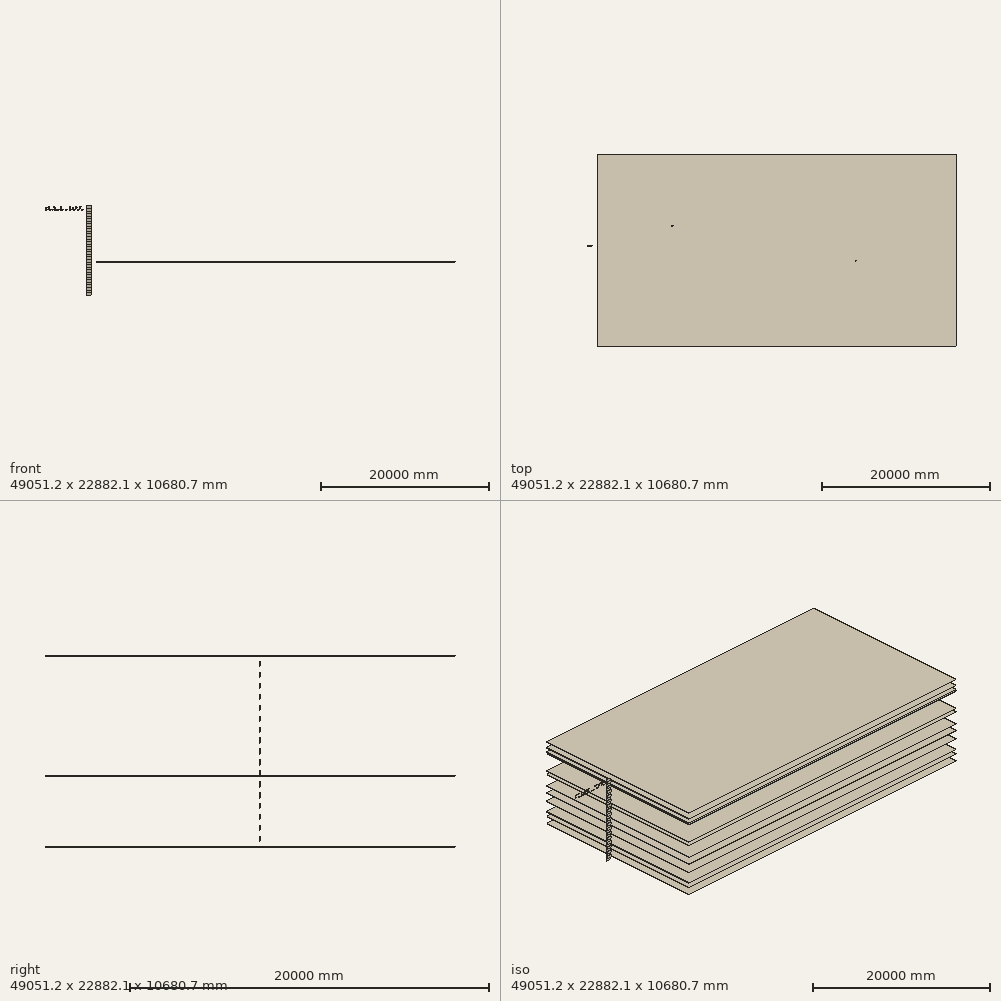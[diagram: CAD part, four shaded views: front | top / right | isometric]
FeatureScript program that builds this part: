
annotation { "Feature Type Name" : "Feature", "Feature Type Description" : "" }
export const myFeature = defineFeature(function(context is Context, id is Id, definition is map)
    precondition{}
    {
        {
            var Q0;
            Q0=qCreatedBy(makeId("Top.planeOp"),FACE);
            var sketch = newSketch(context, id + "F0", { "sketchPlane" : qUnion([Q0])});
            skLineSegment(sketch, "E0.bottom", {"start": v(-13590.57, 10870.04) * mm, "end": v(29302.01, 10870.04) * mm});
            skLineSegment(sketch, "E0.top", {"start": v(-13590.57, -12012.05) * mm, "end": v(29302.01, -12012.05) * mm});
            skLineSegment(sketch, "E0.left", {"start": v(-13590.57, 10870.04) * mm, "end": v(-13590.57, -12012.05) * mm});
            skLineSegment(sketch, "E0.right", {"start": v(29302.01, 10870.04) * mm, "end": v(29302.01, -12012.05) * mm});
            skSolve(sketch);
        }
        {
            var Q0;
            Q0=qSketchRegion(id+"F0",true);
            extrude(context, id + "F1", {"entities" : qUnion([Q0]), "depth" : 12.7 * mm});
        }
        {
            var Q0;
            Q0=makeQuery(id+"F1.opExtrude","SWEPT_BODY",BODY,{"disambiguationData":[OSD([sQuery(id+"F0.wireOp",EDGE,"E0.bottom"),sQuery(id+"F0.wireOp",EDGE,"E0.top"),sQuery(id+"F0.wireOp",EDGE,"E0.left"),sQuery(id+"F0.wireOp",EDGE,"E0.right")])]});
            transform(context, id + "F2", {"entities" : qUnion([Q0]), "transformType" : TransformType.TRANSLATION_3D, "dx" : 0 * mm, "dy" : 0 * mm, "dz" : -762 * mm, "makeCopy" : true});
        }
        {
            var Q0;
            Q0=makeQuery(id+"F1.opExtrude","SWEPT_BODY",BODY,{"disambiguationData":[OSD([sQuery(id+"F0.wireOp",EDGE,"E0.bottom"),sQuery(id+"F0.wireOp",EDGE,"E0.top"),sQuery(id+"F0.wireOp",EDGE,"E0.left"),sQuery(id+"F0.wireOp",EDGE,"E0.right")])]});
            transform(context, id + "F3", {"entities" : qUnion([Q0]), "transformType" : TransformType.TRANSLATION_3D, "dx" : 0 * mm, "dy" : 0 * mm, "dz" : -1295.4 * mm, "makeCopy" : true});
        }
        {
            var Q0;
            Q0=makeQuery(id+"F1.opExtrude","SWEPT_BODY",BODY,{"disambiguationData":[OSD([sQuery(id+"F0.wireOp",EDGE,"E0.bottom"),sQuery(id+"F0.wireOp",EDGE,"E0.top"),sQuery(id+"F0.wireOp",EDGE,"E0.left"),sQuery(id+"F0.wireOp",EDGE,"E0.right")])]});
            transform(context, id + "F4", {"entities" : qUnion([Q0]), "transformType" : TransformType.TRANSLATION_3D, "dx" : 0 * mm, "dy" : 0 * mm, "dz" : -1524 * mm, "makeCopy" : true});
        }
        {
            var Q0;
            Q0=makeQuery(id+"F1.opExtrude","SWEPT_BODY",BODY,{"disambiguationData":[OSD([sQuery(id+"F0.wireOp",EDGE,"E0.bottom"),sQuery(id+"F0.wireOp",EDGE,"E0.top"),sQuery(id+"F0.wireOp",EDGE,"E0.left"),sQuery(id+"F0.wireOp",EDGE,"E0.right")])]});
            transform(context, id + "F5", {"entities" : qUnion([Q0]), "transformType" : TransformType.TRANSLATION_3D, "dx" : 0 * mm, "dy" : 0 * mm, "dz" : -3810 * mm, "makeCopy" : true});
        }
        {
            var Q0;
            Q0=makeQuery(id+"F1.opExtrude","SWEPT_BODY",BODY,{"disambiguationData":[OSD([sQuery(id+"F0.wireOp",EDGE,"E0.bottom"),sQuery(id+"F0.wireOp",EDGE,"E0.top"),sQuery(id+"F0.wireOp",EDGE,"E0.left"),sQuery(id+"F0.wireOp",EDGE,"E0.right")])]});
            transform(context, id + "F6", {"entities" : qUnion([Q0]), "transformType" : TransformType.TRANSLATION_3D, "dx" : 0 * mm, "dy" : 0 * mm, "dz" : -4267.2 * mm, "makeCopy" : true});
        }
        {
            var Q0;
            Q0=makeQuery(id+"F1.opExtrude","SWEPT_BODY",BODY,{"disambiguationData":[OSD([sQuery(id+"F0.wireOp",EDGE,"E0.bottom"),sQuery(id+"F0.wireOp",EDGE,"E0.top"),sQuery(id+"F0.wireOp",EDGE,"E0.left"),sQuery(id+"F0.wireOp",EDGE,"E0.right")])]});
            transform(context, id + "F7", {"entities" : qUnion([Q0]), "transformType" : TransformType.TRANSLATION_3D, "dx" : 0 * mm, "dy" : 0 * mm, "dz" : -5791.2 * mm, "makeCopy" : true});
        }
        {
            var Q0;
            Q0=makeQuery(id+"F1.opExtrude","SWEPT_BODY",BODY,{"disambiguationData":[OSD([sQuery(id+"F0.wireOp",EDGE,"E0.bottom"),sQuery(id+"F0.wireOp",EDGE,"E0.top"),sQuery(id+"F0.wireOp",EDGE,"E0.left"),sQuery(id+"F0.wireOp",EDGE,"E0.right")])]});
            transform(context, id + "F8", {"entities" : qUnion([Q0]), "transformType" : TransformType.TRANSLATION_3D, "dx" : 0 * mm, "dy" : 0 * mm, "dz" : -6705.6 * mm, "makeCopy" : true});
        }
        {
            var Q0;
            Q0=makeQuery(id+"F1.opExtrude","SWEPT_BODY",BODY,{"disambiguationData":[OSD([sQuery(id+"F0.wireOp",EDGE,"E0.bottom"),sQuery(id+"F0.wireOp",EDGE,"E0.top"),sQuery(id+"F0.wireOp",EDGE,"E0.left"),sQuery(id+"F0.wireOp",EDGE,"E0.right")])]});
            transform(context, id + "F9", {"entities" : qUnion([Q0]), "transformType" : TransformType.TRANSLATION_3D, "dx" : 0 * mm, "dy" : 0 * mm, "dz" : -7772.4 * mm, "makeCopy" : true});
        }
        {
            var Q0;
            Q0=makeQuery(id+"F1.opExtrude","SWEPT_BODY",BODY,{"disambiguationData":[OSD([sQuery(id+"F0.wireOp",EDGE,"E0.bottom"),sQuery(id+"F0.wireOp",EDGE,"E0.top"),sQuery(id+"F0.wireOp",EDGE,"E0.left"),sQuery(id+"F0.wireOp",EDGE,"E0.right")])]});
            transform(context, id + "F10", {"entities" : qUnion([Q0]), "transformType" : TransformType.TRANSLATION_3D, "dx" : 0 * mm, "dy" : 0 * mm, "dz" : -9144 * mm, "makeCopy" : true});
        }
        {
            var Q0;
            Q0=makeQuery(id+"F1.opExtrude","SWEPT_BODY",BODY,{"disambiguationData":[OSD([sQuery(id+"F0.wireOp",EDGE,"E0.bottom"),sQuery(id+"F0.wireOp",EDGE,"E0.top"),sQuery(id+"F0.wireOp",EDGE,"E0.left"),sQuery(id+"F0.wireOp",EDGE,"E0.right")])]});
            transform(context, id + "F11", {"entities" : qUnion([Q0]), "transformType" : TransformType.TRANSLATION_3D, "dx" : 0 * mm, "dy" : 0 * mm, "dz" : -9753.6 * mm, "makeCopy" : true});
        }
        {
            var Q0;
            Q0=makeQuery(id+"F1.opExtrude","SWEPT_BODY",BODY,{"disambiguationData":[OSD([sQuery(id+"F0.wireOp",EDGE,"E0.bottom"),sQuery(id+"F0.wireOp",EDGE,"E0.top"),sQuery(id+"F0.wireOp",EDGE,"E0.left"),sQuery(id+"F0.wireOp",EDGE,"E0.right")])]});
            transform(context, id + "F12", {"entities" : qUnion([Q0]), "transformType" : TransformType.TRANSLATION_3D, "dx" : 0 * mm, "dy" : 0 * mm, "dz" : -10668 * mm, "makeCopy" : true});
        }
        {
            var Q0;
            Q0=makeQuery(id+"F1.opExtrude","CAP_FACE",FACE,{"disambiguationData":[OSD([sQuery(id+"F0.wireOp",EDGE,"E0.bottom"),sQuery(id+"F0.wireOp",EDGE,"E0.top"),sQuery(id+"F0.wireOp",EDGE,"E0.left"),sQuery(id+"F0.wireOp",EDGE,"E0.right")])],"isStart":false});
            var sketch = newSketch(context, id + "F13", { "sketchPlane" : qUnion([Q0])});
            skCircle(sketch, "E1", {"center": v(-4667.52, 2370.02) * mm, "radius": 76.2 * mm});
            skCircle(sketch, "E2", {"center": v(17228.5, -1797.32) * mm, "radius": 76.2 * mm});
            skSolve(sketch);
        }
        {
            var Q0;
            Q0=qSketchRegion(id+"F13",true);
            extrude(context, id + "F14", {"entities" : qUnion([Q0]), "operationType" : NewBodyOperationType.REMOVE, "endBound" : BoundingType.THROUGH_ALL, "oppositeDirection" : true, "depth" : 30.48 * mm});
        }
        {
            var Q0;
            Q0=qCreatedBy(makeId("Front.planeOp"),FACE);
            var sketch = newSketch(context, id + "F15", { "sketchPlane" : qUnion([Q0])});
            skLineSegment(sketch, "E3.bottom", {"start": v(-14200.17, 0) * mm, "end": v(-14809.77, 0) * mm});
            skLineSegment(sketch, "E3.top", {"start": v(-14200.17, -304.8) * mm, "end": v(-14809.77, -304.8) * mm});
            skLineSegment(sketch, "E3.left", {"start": v(-14200.17, 0) * mm, "end": v(-14200.17, -304.8) * mm});
            skLineSegment(sketch, "E3.right", {"start": v(-14809.77, 0) * mm, "end": v(-14809.77, -304.8) * mm});
            skLineSegment(sketch, "E4.0.1.0", {"start": v(-14200.17, -609.6) * mm, "end": v(-14809.77, -609.6) * mm});
            skLineSegment(sketch, "E4.0.1.1", {"start": v(-14200.17, -304.8) * mm, "end": v(-14200.17, -609.6) * mm});
            skLineSegment(sketch, "E4.0.1.2", {"start": v(-14809.77, -304.8) * mm, "end": v(-14809.77, -609.6) * mm});
            skLineSegment(sketch, "E4.direction1", {"start": v(-14809.77, -304.8) * mm, "end": v(-14600.97, -304.8) * mm, "construction": true});
            skLineSegment(sketch, "E4.direction2", {"start": v(-14809.77, -304.8) * mm, "end": v(-14809.77, -609.6) * mm, "construction": true});
            skLineSegment(sketch, "E5.0.0.2", {"start": v(-14200.17, -914.4) * mm, "end": v(-14809.77, -914.4) * mm});
            skLineSegment(sketch, "E5.3.0.2", {"start": v(-14200.17, -609.6) * mm, "end": v(-14200.17, -914.4) * mm});
            skLineSegment(sketch, "E5.6.0.2", {"start": v(-14809.77, -609.6) * mm, "end": v(-14809.77, -914.4) * mm});
            skLineSegment(sketch, "E5.0.0.3", {"start": v(-14200.17, -1219.2) * mm, "end": v(-14809.77, -1219.2) * mm});
            skLineSegment(sketch, "E5.3.0.3", {"start": v(-14200.17, -914.4) * mm, "end": v(-14200.17, -1219.2) * mm});
            skLineSegment(sketch, "E5.6.0.3", {"start": v(-14809.77, -914.4) * mm, "end": v(-14809.77, -1219.2) * mm});
            skLineSegment(sketch, "E5.0.0.4", {"start": v(-14200.17, -1524) * mm, "end": v(-14809.77, -1524) * mm});
            skLineSegment(sketch, "E5.3.0.4", {"start": v(-14200.17, -1219.2) * mm, "end": v(-14200.17, -1524) * mm});
            skLineSegment(sketch, "E5.6.0.4", {"start": v(-14809.77, -1219.2) * mm, "end": v(-14809.77, -1524) * mm});
            skLineSegment(sketch, "E5.0.0.5", {"start": v(-14200.17, -1828.8) * mm, "end": v(-14809.77, -1828.8) * mm});
            skLineSegment(sketch, "E5.3.0.5", {"start": v(-14200.17, -1524) * mm, "end": v(-14200.17, -1828.8) * mm});
            skLineSegment(sketch, "E5.6.0.5", {"start": v(-14809.77, -1524) * mm, "end": v(-14809.77, -1828.8) * mm});
            skLineSegment(sketch, "E5.0.0.6", {"start": v(-14200.17, -2133.6) * mm, "end": v(-14809.77, -2133.6) * mm});
            skLineSegment(sketch, "E5.3.0.6", {"start": v(-14200.17, -1828.8) * mm, "end": v(-14200.17, -2133.6) * mm});
            skLineSegment(sketch, "E5.6.0.6", {"start": v(-14809.77, -1828.8) * mm, "end": v(-14809.77, -2133.6) * mm});
            skLineSegment(sketch, "E5.0.0.7", {"start": v(-14200.17, -2438.4) * mm, "end": v(-14809.77, -2438.4) * mm});
            skLineSegment(sketch, "E5.3.0.7", {"start": v(-14200.17, -2133.6) * mm, "end": v(-14200.17, -2438.4) * mm});
            skLineSegment(sketch, "E5.6.0.7", {"start": v(-14809.77, -2133.6) * mm, "end": v(-14809.77, -2438.4) * mm});
            skLineSegment(sketch, "E5.0.0.8", {"start": v(-14200.17, -2743.2) * mm, "end": v(-14809.77, -2743.2) * mm});
            skLineSegment(sketch, "E5.3.0.8", {"start": v(-14200.17, -2438.4) * mm, "end": v(-14200.17, -2743.2) * mm});
            skLineSegment(sketch, "E5.6.0.8", {"start": v(-14809.77, -2438.4) * mm, "end": v(-14809.77, -2743.2) * mm});
            skLineSegment(sketch, "E5.0.0.9", {"start": v(-14200.17, -3048) * mm, "end": v(-14809.77, -3048) * mm});
            skLineSegment(sketch, "E5.3.0.9", {"start": v(-14200.17, -2743.2) * mm, "end": v(-14200.17, -3048) * mm});
            skLineSegment(sketch, "E5.6.0.9", {"start": v(-14809.77, -2743.2) * mm, "end": v(-14809.77, -3048) * mm});
            skLineSegment(sketch, "E5.0.0.10", {"start": v(-14200.17, -3352.8) * mm, "end": v(-14809.77, -3352.8) * mm});
            skLineSegment(sketch, "E5.3.0.10", {"start": v(-14200.17, -3048) * mm, "end": v(-14200.17, -3352.8) * mm});
            skLineSegment(sketch, "E5.6.0.10", {"start": v(-14809.77, -3048) * mm, "end": v(-14809.77, -3352.8) * mm});
            skLineSegment(sketch, "E5.0.0.11", {"start": v(-14200.17, -3657.6) * mm, "end": v(-14809.77, -3657.6) * mm});
            skLineSegment(sketch, "E5.3.0.11", {"start": v(-14200.17, -3352.8) * mm, "end": v(-14200.17, -3657.6) * mm});
            skLineSegment(sketch, "E5.6.0.11", {"start": v(-14809.77, -3352.8) * mm, "end": v(-14809.77, -3657.6) * mm});
            skLineSegment(sketch, "E5.0.0.12", {"start": v(-14200.17, -3962.4) * mm, "end": v(-14809.77, -3962.4) * mm});
            skLineSegment(sketch, "E5.3.0.12", {"start": v(-14200.17, -3657.6) * mm, "end": v(-14200.17, -3962.4) * mm});
            skLineSegment(sketch, "E5.6.0.12", {"start": v(-14809.77, -3657.6) * mm, "end": v(-14809.77, -3962.4) * mm});
            skLineSegment(sketch, "E5.0.0.13", {"start": v(-14200.17, -4267.2) * mm, "end": v(-14809.77, -4267.2) * mm});
            skLineSegment(sketch, "E5.3.0.13", {"start": v(-14200.17, -3962.4) * mm, "end": v(-14200.17, -4267.2) * mm});
            skLineSegment(sketch, "E5.6.0.13", {"start": v(-14809.77, -3962.4) * mm, "end": v(-14809.77, -4267.2) * mm});
            skLineSegment(sketch, "E5.0.0.14", {"start": v(-14200.17, -4572) * mm, "end": v(-14809.77, -4572) * mm});
            skLineSegment(sketch, "E5.3.0.14", {"start": v(-14200.17, -4267.2) * mm, "end": v(-14200.17, -4572) * mm});
            skLineSegment(sketch, "E5.6.0.14", {"start": v(-14809.77, -4267.2) * mm, "end": v(-14809.77, -4572) * mm});
            skLineSegment(sketch, "E5.0.0.15", {"start": v(-14200.17, -4876.8) * mm, "end": v(-14809.77, -4876.8) * mm});
            skLineSegment(sketch, "E5.3.0.15", {"start": v(-14200.17, -4572) * mm, "end": v(-14200.17, -4876.8) * mm});
            skLineSegment(sketch, "E5.6.0.15", {"start": v(-14809.77, -4572) * mm, "end": v(-14809.77, -4876.8) * mm});
            skLineSegment(sketch, "E5.0.0.16", {"start": v(-14200.17, -5181.6) * mm, "end": v(-14809.77, -5181.6) * mm});
            skLineSegment(sketch, "E5.3.0.16", {"start": v(-14200.17, -4876.8) * mm, "end": v(-14200.17, -5181.6) * mm});
            skLineSegment(sketch, "E5.6.0.16", {"start": v(-14809.77, -4876.8) * mm, "end": v(-14809.77, -5181.6) * mm});
            skLineSegment(sketch, "E5.0.0.17", {"start": v(-14200.17, -5486.4) * mm, "end": v(-14809.77, -5486.4) * mm});
            skLineSegment(sketch, "E5.3.0.17", {"start": v(-14200.17, -5181.6) * mm, "end": v(-14200.17, -5486.4) * mm});
            skLineSegment(sketch, "E5.6.0.17", {"start": v(-14809.77, -5181.6) * mm, "end": v(-14809.77, -5486.4) * mm});
            skLineSegment(sketch, "E5.0.0.18", {"start": v(-14200.17, -5791.2) * mm, "end": v(-14809.77, -5791.2) * mm});
            skLineSegment(sketch, "E5.3.0.18", {"start": v(-14200.17, -5486.4) * mm, "end": v(-14200.17, -5791.2) * mm});
            skLineSegment(sketch, "E5.6.0.18", {"start": v(-14809.77, -5486.4) * mm, "end": v(-14809.77, -5791.2) * mm});
            skLineSegment(sketch, "E5.0.0.19", {"start": v(-14200.17, -6096) * mm, "end": v(-14809.77, -6096) * mm});
            skLineSegment(sketch, "E5.3.0.19", {"start": v(-14200.17, -5791.2) * mm, "end": v(-14200.17, -6096) * mm});
            skLineSegment(sketch, "E5.6.0.19", {"start": v(-14809.77, -5791.2) * mm, "end": v(-14809.77, -6096) * mm});
            skLineSegment(sketch, "E6.0.0.20", {"start": v(-14200.17, -6400.8) * mm, "end": v(-14809.77, -6400.8) * mm});
            skLineSegment(sketch, "E6.3.0.20", {"start": v(-14200.17, -6096) * mm, "end": v(-14200.17, -6400.8) * mm});
            skLineSegment(sketch, "E6.6.0.20", {"start": v(-14809.77, -6096) * mm, "end": v(-14809.77, -6400.8) * mm});
            skLineSegment(sketch, "E6.0.0.21", {"start": v(-14200.17, -6705.6) * mm, "end": v(-14809.77, -6705.6) * mm});
            skLineSegment(sketch, "E6.3.0.21", {"start": v(-14200.17, -6400.8) * mm, "end": v(-14200.17, -6705.6) * mm});
            skLineSegment(sketch, "E6.6.0.21", {"start": v(-14809.77, -6400.8) * mm, "end": v(-14809.77, -6705.6) * mm});
            skLineSegment(sketch, "E6.0.0.22", {"start": v(-14200.17, -7010.4) * mm, "end": v(-14809.77, -7010.4) * mm});
            skLineSegment(sketch, "E6.3.0.22", {"start": v(-14200.17, -6705.6) * mm, "end": v(-14200.17, -7010.4) * mm});
            skLineSegment(sketch, "E6.6.0.22", {"start": v(-14809.77, -6705.6) * mm, "end": v(-14809.77, -7010.4) * mm});
            skLineSegment(sketch, "E6.0.0.23", {"start": v(-14200.17, -7315.2) * mm, "end": v(-14809.77, -7315.2) * mm});
            skLineSegment(sketch, "E6.3.0.23", {"start": v(-14200.17, -7010.4) * mm, "end": v(-14200.17, -7315.2) * mm});
            skLineSegment(sketch, "E6.6.0.23", {"start": v(-14809.77, -7010.4) * mm, "end": v(-14809.77, -7315.2) * mm});
            skLineSegment(sketch, "E6.0.0.24", {"start": v(-14200.17, -7620) * mm, "end": v(-14809.77, -7620) * mm});
            skLineSegment(sketch, "E6.3.0.24", {"start": v(-14200.17, -7315.2) * mm, "end": v(-14200.17, -7620) * mm});
            skLineSegment(sketch, "E6.6.0.24", {"start": v(-14809.77, -7315.2) * mm, "end": v(-14809.77, -7620) * mm});
            skLineSegment(sketch, "E6.0.0.25", {"start": v(-14200.17, -7924.8) * mm, "end": v(-14809.77, -7924.8) * mm});
            skLineSegment(sketch, "E6.3.0.25", {"start": v(-14200.17, -7620) * mm, "end": v(-14200.17, -7924.8) * mm});
            skLineSegment(sketch, "E6.6.0.25", {"start": v(-14809.77, -7620) * mm, "end": v(-14809.77, -7924.8) * mm});
            skLineSegment(sketch, "E6.0.0.26", {"start": v(-14200.17, -8229.6) * mm, "end": v(-14809.77, -8229.6) * mm});
            skLineSegment(sketch, "E6.3.0.26", {"start": v(-14200.17, -7924.8) * mm, "end": v(-14200.17, -8229.6) * mm});
            skLineSegment(sketch, "E6.6.0.26", {"start": v(-14809.77, -7924.8) * mm, "end": v(-14809.77, -8229.6) * mm});
            skLineSegment(sketch, "E6.0.0.27", {"start": v(-14200.17, -8534.4) * mm, "end": v(-14809.77, -8534.4) * mm});
            skLineSegment(sketch, "E6.3.0.27", {"start": v(-14200.17, -8229.6) * mm, "end": v(-14200.17, -8534.4) * mm});
            skLineSegment(sketch, "E6.6.0.27", {"start": v(-14809.77, -8229.6) * mm, "end": v(-14809.77, -8534.4) * mm});
            skLineSegment(sketch, "E6.0.0.28", {"start": v(-14200.17, -8839.2) * mm, "end": v(-14809.77, -8839.2) * mm});
            skLineSegment(sketch, "E6.3.0.28", {"start": v(-14200.17, -8534.4) * mm, "end": v(-14200.17, -8839.2) * mm});
            skLineSegment(sketch, "E6.6.0.28", {"start": v(-14809.77, -8534.4) * mm, "end": v(-14809.77, -8839.2) * mm});
            skLineSegment(sketch, "E6.0.0.29", {"start": v(-14200.17, -9144) * mm, "end": v(-14809.77, -9144) * mm});
            skLineSegment(sketch, "E6.3.0.29", {"start": v(-14200.17, -8839.2) * mm, "end": v(-14200.17, -9144) * mm});
            skLineSegment(sketch, "E6.6.0.29", {"start": v(-14809.77, -8839.2) * mm, "end": v(-14809.77, -9144) * mm});
            skLineSegment(sketch, "E6.0.0.30", {"start": v(-14200.17, -9448.8) * mm, "end": v(-14809.77, -9448.8) * mm});
            skLineSegment(sketch, "E6.3.0.30", {"start": v(-14200.17, -9144) * mm, "end": v(-14200.17, -9448.8) * mm});
            skLineSegment(sketch, "E6.6.0.30", {"start": v(-14809.77, -9144) * mm, "end": v(-14809.77, -9448.8) * mm});
            skLineSegment(sketch, "E6.0.0.31", {"start": v(-14200.17, -9753.6) * mm, "end": v(-14809.77, -9753.6) * mm});
            skLineSegment(sketch, "E6.3.0.31", {"start": v(-14200.17, -9448.8) * mm, "end": v(-14200.17, -9753.6) * mm});
            skLineSegment(sketch, "E6.6.0.31", {"start": v(-14809.77, -9448.8) * mm, "end": v(-14809.77, -9753.6) * mm});
            skLineSegment(sketch, "E6.0.0.32", {"start": v(-14200.17, -10058.4) * mm, "end": v(-14809.77, -10058.4) * mm});
            skLineSegment(sketch, "E6.3.0.32", {"start": v(-14200.17, -9753.6) * mm, "end": v(-14200.17, -10058.4) * mm});
            skLineSegment(sketch, "E6.6.0.32", {"start": v(-14809.77, -9753.6) * mm, "end": v(-14809.77, -10058.4) * mm});
            skLineSegment(sketch, "E6.0.0.33", {"start": v(-14200.17, -10363.2) * mm, "end": v(-14809.77, -10363.2) * mm});
            skLineSegment(sketch, "E6.3.0.33", {"start": v(-14200.17, -10058.4) * mm, "end": v(-14200.17, -10363.2) * mm});
            skLineSegment(sketch, "E6.6.0.33", {"start": v(-14809.77, -10058.4) * mm, "end": v(-14809.77, -10363.2) * mm});
            skLineSegment(sketch, "E6.0.0.34", {"start": v(-14200.17, -10668) * mm, "end": v(-14809.77, -10668) * mm});
            skLineSegment(sketch, "E6.3.0.34", {"start": v(-14200.17, -10363.2) * mm, "end": v(-14200.17, -10668) * mm});
            skLineSegment(sketch, "E6.6.0.34", {"start": v(-14809.77, -10363.2) * mm, "end": v(-14809.77, -10668) * mm});
            skSolve(sketch);
        }
        {
            var Q0;
            Q0=qCreatedBy(makeId("Front.planeOp"),FACE);
            var sketch = newSketch(context, id + "F16", { "sketchPlane" : qUnion([Q0])});
            skText(sketch, "E7", { "text": "SCALE 1 FOOT", "fontName": "Tinos-Regular.ttf"});
            const initialGuessF16  = {"E7": [-19.79556, -0.4993, 1, 0, 0.4993]};
            skSetInitialGuess(sketch, initialGuessF16);
            skSolve(sketch);
        }
        {
            var Q0;
            Q0=makeQuery(id+"F16.imprint","IMPRINT",FACE,{"disambiguationData":[TD([[makeQuery(id+"F16.imprint","IMPRINT",EDGE,{"derivedFrom":sQuery(id+"F16.wireOp",EDGE,"E7.sketch_text.stroke-0")}),-1.0]])]});
            var Q1;
            Q1=makeQuery(id+"F16.imprint","IMPRINT",FACE,{"disambiguationData":[TD([[makeQuery(id+"F16.imprint","IMPRINT",EDGE,{"derivedFrom":sQuery(id+"F16.wireOp",EDGE,"E7.sketch_text.stroke-36")}),-1.0]])]});
            var Q2;
            Q2=makeQuery(id+"F16.imprint","IMPRINT",FACE,{"disambiguationData":[TD([[makeQuery(id+"F16.imprint","IMPRINT",EDGE,{"derivedFrom":sQuery(id+"F16.wireOp",EDGE,"E7.sketch_text.stroke-56")}),-1.0]])]});
            var Q3;
            Q3=makeQuery(id+"F16.imprint","IMPRINT",FACE,{"disambiguationData":[TD([[makeQuery(id+"F16.imprint","IMPRINT",EDGE,{"derivedFrom":sQuery(id+"F16.wireOp",EDGE,"E7.sketch_text.stroke-75")}),-1.0]])]});
            var Q4;
            Q4=makeQuery(id+"F16.imprint","IMPRINT",FACE,{"disambiguationData":[TD([[makeQuery(id+"F16.imprint","IMPRINT",EDGE,{"derivedFrom":sQuery(id+"F16.wireOp",EDGE,"E7.sketch_text.stroke-90")}),-1.0]])]});
            var Q5;
            Q5=makeQuery(id+"F16.imprint","IMPRINT",FACE,{"disambiguationData":[TD([[makeQuery(id+"F16.imprint","IMPRINT",EDGE,{"derivedFrom":sQuery(id+"F16.wireOp",EDGE,"E7.sketch_text.stroke-116")}),-1.0]])]});
            var Q6;
            Q6=makeQuery(id+"F16.imprint","IMPRINT",FACE,{"disambiguationData":[TD([[makeQuery(id+"F16.imprint","IMPRINT",EDGE,{"derivedFrom":sQuery(id+"F16.wireOp",EDGE,"E7.sketch_text.stroke-165")}),-1.0]])]});
            var Q7;
            Q7=makeQuery(id+"F16.imprint","IMPRINT",FACE,{"disambiguationData":[TD([[makeQuery(id+"F16.imprint","IMPRINT",EDGE,{"derivedFrom":sQuery(id+"F16.wireOp",EDGE,"E7.sketch_text.stroke-180")}),-1.0]])]});
            var Q8;
            Q8=makeQuery(id+"F16.imprint","IMPRINT",FACE,{"disambiguationData":[TD([[makeQuery(id+"F16.imprint","IMPRINT",EDGE,{"derivedFrom":sQuery(id+"F16.wireOp",EDGE,"E7.sketch_text.stroke-150")}),-1.0]])]});
            var Q9;
            Q9=makeQuery(id+"F16.imprint","IMPRINT",FACE,{"disambiguationData":[TD([[makeQuery(id+"F16.imprint","IMPRINT",EDGE,{"derivedFrom":sQuery(id+"F16.wireOp",EDGE,"E7.sketch_text.stroke-127")}),-1.0]])]});
            extrude(context, id + "F17", {"entities" : qUnion([Q0, Q1, Q2, Q3, Q4, Q5, Q6, Q7, Q8, Q9]), "depth" : 30.48 * mm});
        }
        {
            var Q0;
            Q0=makeQuery(id+"F15.imprint","IMPRINT",FACE,{"disambiguationData":[TD([[makeQuery(id+"F15.imprint","IMPRINT",EDGE,{"derivedFrom":sQuery(id+"F15.wireOp",EDGE,"E3.bottom")}),1.0]])]});
            var Q1;
            Q1=makeQuery(id+"F15.imprint","IMPRINT",FACE,{"disambiguationData":[TD([[makeQuery(id+"F15.imprint","IMPRINT",EDGE,{"derivedFrom":sQuery(id+"F15.wireOp",EDGE,"E4.0.1.0")}),1.0]])]});
            var Q2;
            Q2=makeQuery(id+"F15.imprint","IMPRINT",FACE,{"disambiguationData":[TD([[makeQuery(id+"F15.imprint","IMPRINT",EDGE,{"derivedFrom":sQuery(id+"F15.wireOp",EDGE,"E5.0.0.3")}),1.0]])]});
            var Q3;
            Q3=makeQuery(id+"F15.imprint","IMPRINT",FACE,{"disambiguationData":[TD([[makeQuery(id+"F15.imprint","IMPRINT",EDGE,{"derivedFrom":sQuery(id+"F15.wireOp",EDGE,"E5.0.0.5")}),1.0]])]});
            var Q4;
            Q4=makeQuery(id+"F15.imprint","IMPRINT",FACE,{"disambiguationData":[TD([[makeQuery(id+"F15.imprint","IMPRINT",EDGE,{"derivedFrom":sQuery(id+"F15.wireOp",EDGE,"E5.0.0.7")}),1.0]])]});
            var Q5;
            Q5=makeQuery(id+"F15.imprint","IMPRINT",FACE,{"disambiguationData":[TD([[makeQuery(id+"F15.imprint","IMPRINT",EDGE,{"derivedFrom":sQuery(id+"F15.wireOp",EDGE,"E5.0.0.9")}),1.0]])]});
            var Q6;
            Q6=makeQuery(id+"F15.imprint","IMPRINT",FACE,{"disambiguationData":[TD([[makeQuery(id+"F15.imprint","IMPRINT",EDGE,{"derivedFrom":sQuery(id+"F15.wireOp",EDGE,"E5.0.0.11")}),1.0]])]});
            var Q7;
            Q7=makeQuery(id+"F15.imprint","IMPRINT",FACE,{"disambiguationData":[TD([[makeQuery(id+"F15.imprint","IMPRINT",EDGE,{"derivedFrom":sQuery(id+"F15.wireOp",EDGE,"E5.0.0.13")}),1.0]])]});
            var Q8;
            Q8=makeQuery(id+"F15.imprint","IMPRINT",FACE,{"disambiguationData":[TD([[makeQuery(id+"F15.imprint","IMPRINT",EDGE,{"derivedFrom":sQuery(id+"F15.wireOp",EDGE,"E5.0.0.15")}),1.0]])]});
            var Q9;
            Q9=makeQuery(id+"F15.imprint","IMPRINT",FACE,{"disambiguationData":[TD([[makeQuery(id+"F15.imprint","IMPRINT",EDGE,{"derivedFrom":sQuery(id+"F15.wireOp",EDGE,"E5.0.0.17")}),1.0]])]});
            var Q10;
            Q10=makeQuery(id+"F15.imprint","IMPRINT",FACE,{"disambiguationData":[TD([[makeQuery(id+"F15.imprint","IMPRINT",EDGE,{"derivedFrom":sQuery(id+"F15.wireOp",EDGE,"E5.0.0.19")}),1.0]])]});
            var Q11;
            Q11=makeQuery(id+"F15.imprint","IMPRINT",FACE,{"disambiguationData":[TD([[makeQuery(id+"F15.imprint","IMPRINT",EDGE,{"derivedFrom":sQuery(id+"F15.wireOp",EDGE,"E6.0.0.21")}),1.0]])]});
            var Q12;
            Q12=makeQuery(id+"F15.imprint","IMPRINT",FACE,{"disambiguationData":[TD([[makeQuery(id+"F15.imprint","IMPRINT",EDGE,{"derivedFrom":sQuery(id+"F15.wireOp",EDGE,"E6.0.0.23")}),1.0]])]});
            var Q13;
            Q13=makeQuery(id+"F15.imprint","IMPRINT",FACE,{"disambiguationData":[TD([[makeQuery(id+"F15.imprint","IMPRINT",EDGE,{"derivedFrom":sQuery(id+"F15.wireOp",EDGE,"E6.0.0.27")}),1.0]])]});
            var Q14;
            Q14=makeQuery(id+"F15.imprint","IMPRINT",FACE,{"disambiguationData":[TD([[makeQuery(id+"F15.imprint","IMPRINT",EDGE,{"derivedFrom":sQuery(id+"F15.wireOp",EDGE,"E6.0.0.25")}),1.0]])]});
            var Q15;
            Q15=makeQuery(id+"F15.imprint","IMPRINT",FACE,{"disambiguationData":[TD([[makeQuery(id+"F15.imprint","IMPRINT",EDGE,{"derivedFrom":sQuery(id+"F15.wireOp",EDGE,"E6.0.0.29")}),1.0]])]});
            var Q16;
            Q16=makeQuery(id+"F15.imprint","IMPRINT",FACE,{"disambiguationData":[TD([[makeQuery(id+"F15.imprint","IMPRINT",EDGE,{"derivedFrom":sQuery(id+"F15.wireOp",EDGE,"E6.0.0.31")}),1.0]])]});
            var Q17;
            Q17=makeQuery(id+"F15.imprint","IMPRINT",FACE,{"disambiguationData":[TD([[makeQuery(id+"F15.imprint","IMPRINT",EDGE,{"derivedFrom":sQuery(id+"F15.wireOp",EDGE,"E6.0.0.33")}),1.0]])]});
            extrude(context, id + "F18", {"entities" : qUnion([Q0, Q1, Q2, Q3, Q4, Q5, Q6, Q7, Q8, Q9, Q10, Q11, Q12, Q13, Q14, Q15, Q16, Q17]), "depth" : 30.48 * mm});
        }
        {
            var Q0;
            Q0=makeQuery(id+"F15.imprint","IMPRINT",FACE,{"disambiguationData":[TD([[makeQuery(id+"F15.imprint","IMPRINT",EDGE,{"derivedFrom":sQuery(id+"F15.wireOp",EDGE,"E3.top")}),1.0]])]});
            var Q1;
            Q1=makeQuery(id+"F15.imprint","IMPRINT",FACE,{"disambiguationData":[TD([[makeQuery(id+"F15.imprint","IMPRINT",EDGE,{"derivedFrom":sQuery(id+"F15.wireOp",EDGE,"E5.0.0.2")}),1.0]])]});
            var Q2;
            Q2=makeQuery(id+"F15.imprint","IMPRINT",FACE,{"disambiguationData":[TD([[makeQuery(id+"F15.imprint","IMPRINT",EDGE,{"derivedFrom":sQuery(id+"F15.wireOp",EDGE,"E5.0.0.4")}),1.0]])]});
            var Q3;
            Q3=makeQuery(id+"F15.imprint","IMPRINT",FACE,{"disambiguationData":[TD([[makeQuery(id+"F15.imprint","IMPRINT",EDGE,{"derivedFrom":sQuery(id+"F15.wireOp",EDGE,"E5.0.0.6")}),1.0]])]});
            var Q4;
            Q4=makeQuery(id+"F15.imprint","IMPRINT",FACE,{"disambiguationData":[TD([[makeQuery(id+"F15.imprint","IMPRINT",EDGE,{"derivedFrom":sQuery(id+"F15.wireOp",EDGE,"E5.0.0.8")}),1.0]])]});
            var Q5;
            Q5=makeQuery(id+"F15.imprint","IMPRINT",FACE,{"disambiguationData":[TD([[makeQuery(id+"F15.imprint","IMPRINT",EDGE,{"derivedFrom":sQuery(id+"F15.wireOp",EDGE,"E5.0.0.10")}),1.0]])]});
            var Q6;
            Q6=makeQuery(id+"F15.imprint","IMPRINT",FACE,{"disambiguationData":[TD([[makeQuery(id+"F15.imprint","IMPRINT",EDGE,{"derivedFrom":sQuery(id+"F15.wireOp",EDGE,"E5.0.0.12")}),1.0]])]});
            var Q7;
            Q7=makeQuery(id+"F15.imprint","IMPRINT",FACE,{"disambiguationData":[TD([[makeQuery(id+"F15.imprint","IMPRINT",EDGE,{"derivedFrom":sQuery(id+"F15.wireOp",EDGE,"E5.0.0.14")}),1.0]])]});
            var Q8;
            Q8=makeQuery(id+"F15.imprint","IMPRINT",FACE,{"disambiguationData":[TD([[makeQuery(id+"F15.imprint","IMPRINT",EDGE,{"derivedFrom":sQuery(id+"F15.wireOp",EDGE,"E5.0.0.16")}),1.0]])]});
            var Q9;
            Q9=makeQuery(id+"F15.imprint","IMPRINT",FACE,{"disambiguationData":[TD([[makeQuery(id+"F15.imprint","IMPRINT",EDGE,{"derivedFrom":sQuery(id+"F15.wireOp",EDGE,"E5.0.0.18")}),1.0]])]});
            var Q10;
            Q10=makeQuery(id+"F15.imprint","IMPRINT",FACE,{"disambiguationData":[TD([[makeQuery(id+"F15.imprint","IMPRINT",EDGE,{"derivedFrom":sQuery(id+"F15.wireOp",EDGE,"E6.0.0.20")}),1.0]])]});
            var Q11;
            Q11=makeQuery(id+"F15.imprint","IMPRINT",FACE,{"disambiguationData":[TD([[makeQuery(id+"F15.imprint","IMPRINT",EDGE,{"derivedFrom":sQuery(id+"F15.wireOp",EDGE,"E6.0.0.22")}),1.0]])]});
            var Q12;
            Q12=makeQuery(id+"F15.imprint","IMPRINT",FACE,{"disambiguationData":[TD([[makeQuery(id+"F15.imprint","IMPRINT",EDGE,{"derivedFrom":sQuery(id+"F15.wireOp",EDGE,"E6.0.0.24")}),1.0]])]});
            var Q13;
            Q13=makeQuery(id+"F15.imprint","IMPRINT",FACE,{"disambiguationData":[TD([[makeQuery(id+"F15.imprint","IMPRINT",EDGE,{"derivedFrom":sQuery(id+"F15.wireOp",EDGE,"E6.0.0.26")}),1.0]])]});
            var Q14;
            Q14=makeQuery(id+"F15.imprint","IMPRINT",FACE,{"disambiguationData":[TD([[makeQuery(id+"F15.imprint","IMPRINT",EDGE,{"derivedFrom":sQuery(id+"F15.wireOp",EDGE,"E6.0.0.28")}),1.0]])]});
            var Q15;
            Q15=makeQuery(id+"F15.imprint","IMPRINT",FACE,{"disambiguationData":[TD([[makeQuery(id+"F15.imprint","IMPRINT",EDGE,{"derivedFrom":sQuery(id+"F15.wireOp",EDGE,"E6.0.0.30")}),1.0]])]});
            var Q16;
            Q16=makeQuery(id+"F15.imprint","IMPRINT",FACE,{"disambiguationData":[TD([[makeQuery(id+"F15.imprint","IMPRINT",EDGE,{"derivedFrom":sQuery(id+"F15.wireOp",EDGE,"E6.0.0.32")}),1.0]])]});
            extrude(context, id + "F19", {"entities" : qUnion([Q0, Q1, Q2, Q3, Q4, Q5, Q6, Q7, Q8, Q9, Q10, Q11, Q12, Q13, Q14, Q15, Q16]), "depth" : 91.44 * mm});
        }
    });
